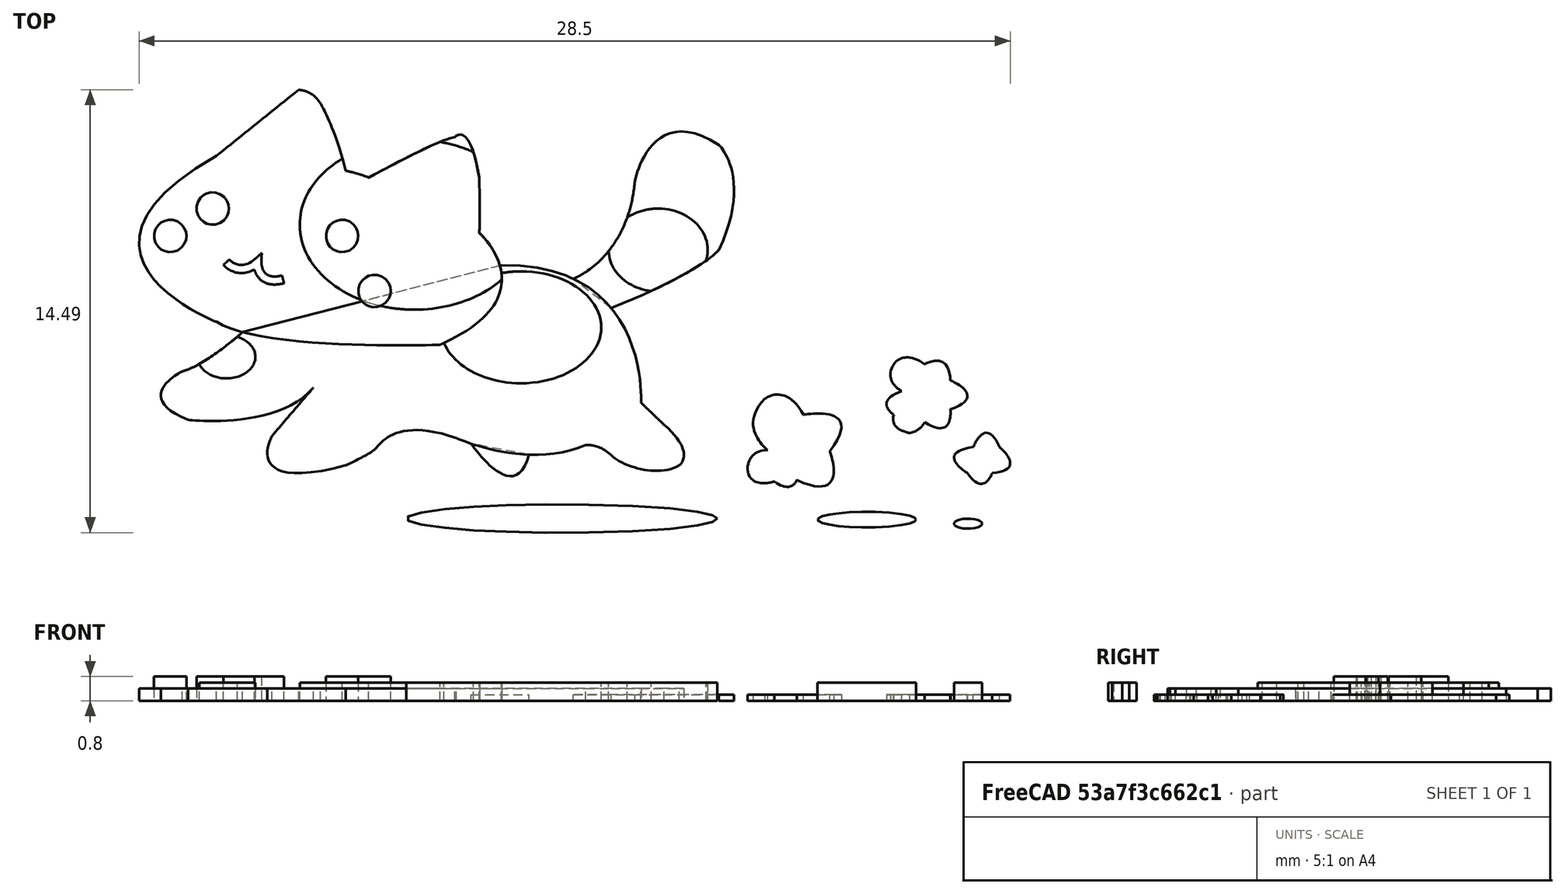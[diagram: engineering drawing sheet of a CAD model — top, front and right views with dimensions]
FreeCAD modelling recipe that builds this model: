
FCSTD DOCUMENT  (FreeCAD 0.19R23756 (Git))
Label: Nyanko09
License: All rights reserved
LicenseURL: http://en.wikipedia.org/wiki/All_rights_reserved
objects: Part::Feature×9, Part::Extrusion×9, App::LinkGroup×1
note: 18 computed .brp shape members not serialized (recipe doc carries the construction recipe); baked Part::Feature solids carry a one-line shape summary decoded from their .brp

FEATURE [Part::Feature] Compound
  shape: bbox 25.61 x 12.78 x 2e-07 mm, 7 faces, 0 solids (baked)
FEATURE [Part::Feature] Face
  shape: bbox 2.264 x 2.021 x 2e-07 mm, 1 faces, 0 solids (baked)
FEATURE [Part::Feature] Face001
  shape: bbox 3.028 x 2.599 x 2e-07 mm, 1 faces, 0 solids (baked)
FEATURE [Part::Feature] Face002
  shape: bbox 3.428 x 3.491 x 2e-07 mm, 1 faces, 0 solids (baked)
FEATURE [Part::Feature] Compound001
  shape: bbox 7.739 x 3.755 x 2e-07 mm, 5 faces, 0 solids (baked)
FEATURE [Part::Feature] Face003
  shape: bbox 13.49 x 8.555 x 2e-07 mm, 1 faces, 0 solids (baked)
FEATURE [Part::Feature] Face004
  shape: bbox 5.526 x 6.176 x 2e-07 mm, 1 faces, 0 solids (baked)
FEATURE [Part::Feature] Face005
  shape: bbox 17.62 x 7.377 x 2e-07 mm, 1 faces, 0 solids (baked)
FEATURE [Part::Feature] Face006
  shape: bbox 1.889 x 1.419 x 2e-07 mm, 1 faces, 0 solids (baked)
FEATURE [Part::Extrusion] Extrude
  Base = -> Compound
  Dir = (0,0,1)
  DirMode = 0
  FaceMakerClass = Part::FaceMakerBullseye
  LengthFwd = 0.6
  LengthRev = 0
  Solid = false
  Symmetric = false
FEATURE [Part::Extrusion] Extrude001
  Base = -> Face
  Dir = (0,0,1)
  DirMode = 0
  FaceMakerClass = Part::FaceMakerBullseye
  LengthFwd = 0.2
  LengthRev = 0
  Solid = false
  Symmetric = false
FEATURE [Part::Extrusion] Extrude002
  Base = -> Face001
  Dir = (0,0,1)
  DirMode = 0
  FaceMakerClass = Part::FaceMakerBullseye
  LengthFwd = 0.2
  LengthRev = 0
  Solid = false
  Symmetric = false
FEATURE [Part::Extrusion] Extrude003
  Base = -> Face002
  Dir = (0,0,1)
  DirMode = 0
  FaceMakerClass = Part::FaceMakerBullseye
  LengthFwd = 0.2
  LengthRev = 0
  Solid = false
  Symmetric = false
FEATURE [Part::Extrusion] Extrude004
  Base = -> Face006
  Dir = (0,0,1)
  DirMode = 0
  FaceMakerClass = Part::FaceMakerBullseye
  LengthFwd = 0.2
  LengthRev = 0
  Solid = false
  Symmetric = false
FEATURE [Part::Extrusion] Extrude005
  Base = -> Face004
  Dir = (0,0,-1)
  DirMode = 2
  FaceMakerClass = Part::FaceMakerBullseye
  LengthFwd = -0.2
  LengthRev = 0
  Solid = false
  Symmetric = false
FEATURE [Part::Extrusion] Extrude006
  Base = -> Compound001
  Dir = (0,0,1)
  DirMode = 0
  FaceMakerClass = Part::FaceMakerBullseye
  LengthFwd = 0.8
  LengthRev = 0
  Solid = false
  Symmetric = false
FEATURE [Part::Extrusion] Extrude007
  Base = -> Face005
  Dir = (0,0,1)
  DirMode = 2
  FaceMakerClass = Part::FaceMakerBullseye
  LengthFwd = 0.4
  LengthRev = 0
  Solid = false
  Symmetric = false
FEATURE [Part::Extrusion] Extrude008
  Base = -> Face003
  Dir = (0,0,-1)
  DirMode = 2
  FaceMakerClass = Part::FaceMakerBullseye
  LengthFwd = -0.4
  LengthRev = 0
  Solid = false
  Symmetric = false
FEATURE [App::LinkGroup] LinkGroup  label="Nyanko"
  ElementList = -> [Extrude,Extrude001,Extrude002,Extrude003,Extrude004,Extrude005,Extrude006,Extrude007,Extrude008]
  LinkMode = 0
